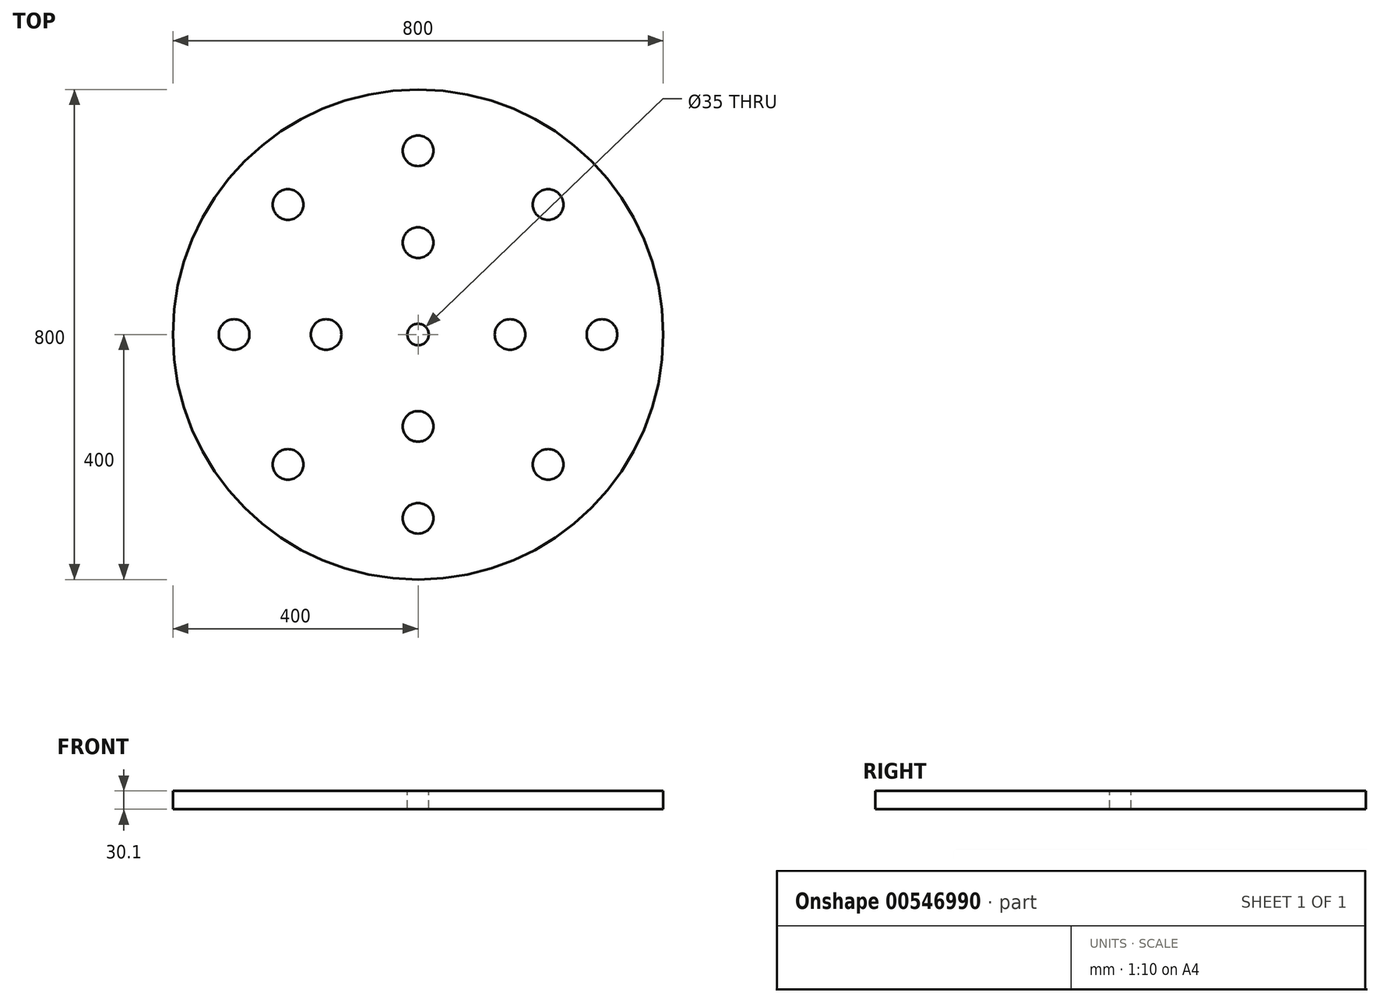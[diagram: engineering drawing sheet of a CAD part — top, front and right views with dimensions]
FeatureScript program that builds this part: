
annotation { "Feature Type Name" : "Feature", "Feature Type Description" : "" }
export const myFeature = defineFeature(function(context is Context, id is Id, definition is map)
    precondition{}
    {
        {
            var Q0;
            Q0=qCreatedBy(makeId("Top.planeOp"),FACE);
            var sketch = newSketch(context, id + "F0", { "sketchPlane" : qUnion([Q0])});
            skCircle(sketch, "E0", {"center": v(0, 0) * mm, "radius": 400 * mm});
            skSolve(sketch);
        }
        {
            var Q0;
            Q0=makeQuery(id+"F0.imprint","IMPRINT",FACE,{"disambiguationData":[TD([[makeQuery(id+"F0.imprint","IMPRINT",EDGE,{"derivedFrom":sQuery(id+"F0.wireOp",EDGE,"E0")}),1.0]])]});
            extrude(context, id + "F1", {"entities" : qUnion([Q0]), "depth" : 30 * mm, "offsetDistance" : 25 * mm});
        }
        {
            var Q0;
            Q0=makeQuery(id+"F1.opExtrude","CAP_FACE",FACE,{"disambiguationData":[OSD([sQuery(id+"F0.wireOp",EDGE,"E0")])],"isStart":false});
            var sketch = newSketch(context, id + "F2", { "sketchPlane" : qUnion([Q0])});
            skCircle(sketch, "E1", {"center": v(0, 0) * mm, "radius": 150 * mm});
            skCircle(sketch, "E2", {"center": v(0, 0) * mm, "radius": 300 * mm});
            skLineSegment(sketch, "E3", {"start": v(0, 408.52) * mm, "end": v(0, -368.47) * mm});
            skLineSegment(sketch, "E4", {"start": v(451, 0) * mm, "end": v(-503.41, 0) * mm});
            skLineSegment(sketch, "E5", {"start": v(-323.18, -323.18) * mm, "end": v(360.31, 360.31) * mm});
            skLineSegment(sketch, "E6", {"start": v(-331.16, 331.16) * mm, "end": v(365.47, -365.47) * mm});
            skSolve(sketch);
        }
        {
            var Q0;
            {var subQ0=sQuery(id+"F2.wireOp",EDGE,"E4");var subQ1=sQuery(id+"F2.wireOp",EDGE,"E1");var subQ2=makeQuery(id+"F2.imprint","INTERSECT",VERTEX,{"disambiguationData":[OD(0.0)],"derivedFrom":[subQ1,subQ0]});Q0=makeQuery(id+"F2.imprint","IMPRINT",FACE,{"disambiguationData":[TD([[makeQuery(id+"F2.imprint","IMPRINT",EDGE,{"disambiguationData":[TD([[subQ2,1.0]])],"derivedFrom":subQ1}),-1.0]])]});}
            var sketch = newSketch(context, id + "F3", { "sketchPlane" : qUnion([Q0])});
            skCircle(sketch, "E7", {"center": v(212.13, 212.13) * mm, "radius": 25 * mm});
            skCircle(sketch, "E8", {"center": v(212.13, -212.13) * mm, "radius": 25 * mm});
            skCircle(sketch, "E9", {"center": v(-212.13, -212.13) * mm, "radius": 25 * mm});
            skCircle(sketch, "E10", {"center": v(-212.13, 212.13) * mm, "radius": 25 * mm});
            skCircle(sketch, "E11", {"center": v(0, 150) * mm, "radius": 25 * mm});
            skCircle(sketch, "E12", {"center": v(0, -150) * mm, "radius": 25 * mm});
            skCircle(sketch, "E13", {"center": v(150, 0) * mm, "radius": 25 * mm});
            skCircle(sketch, "E14", {"center": v(-150, 0) * mm, "radius": 25 * mm});
            skCircle(sketch, "E15", {"center": v(0, 300) * mm, "radius": 25 * mm});
            skCircle(sketch, "E16", {"center": v(300, 0) * mm, "radius": 25 * mm});
            skCircle(sketch, "E17", {"center": v(0, -300) * mm, "radius": 25 * mm});
            skCircle(sketch, "E18", {"center": v(-300, 0) * mm, "radius": 25 * mm});
            skSolve(sketch);
        }
        {
            var Q0;
            Q0 = qSketchRegion(id + "F3", true);
            extrude(context, id + "F4", {"entities" : qUnion([Q0]), "operationType" : NewBodyOperationType.ADD, "depth" : 0.1 * mm, "offsetDistance" : 25 * mm});
        }
        {
            var Q0;
            {var subQ0=sQuery(id+"F2.wireOp",EDGE,"E6");var subQ1=sQuery(id+"F2.wireOp",EDGE,"E1");var subQ2=makeQuery(id+"F2.imprint","INTERSECT",VERTEX,{"disambiguationData":[OD(0.0)],"derivedFrom":[subQ1,subQ0]});Q0=makeQuery(id+"F2.imprint","IMPRINT",FACE,{"disambiguationData":[TD([[makeQuery(id+"F2.imprint","IMPRINT",EDGE,{"disambiguationData":[TD([[subQ2,-1.0]])],"derivedFrom":subQ1}),1.0]])]});}
            var sketch = newSketch(context, id + "F5", { "sketchPlane" : qUnion([Q0])});
            skCircle(sketch, "E19", {"center": v(0, 0) * mm, "radius": 17.5 * mm});
            skSolve(sketch);
        }
        {
            var Q0;
            Q0 = qSketchRegion(id + "F5", true);
            extrude(context, id + "F6", {"entities" : qUnion([Q0]), "operationType" : NewBodyOperationType.REMOVE, "oppositeDirection" : true, "depth" : 60 * mm, "offsetDistance" : 25 * mm});
        }
    });
